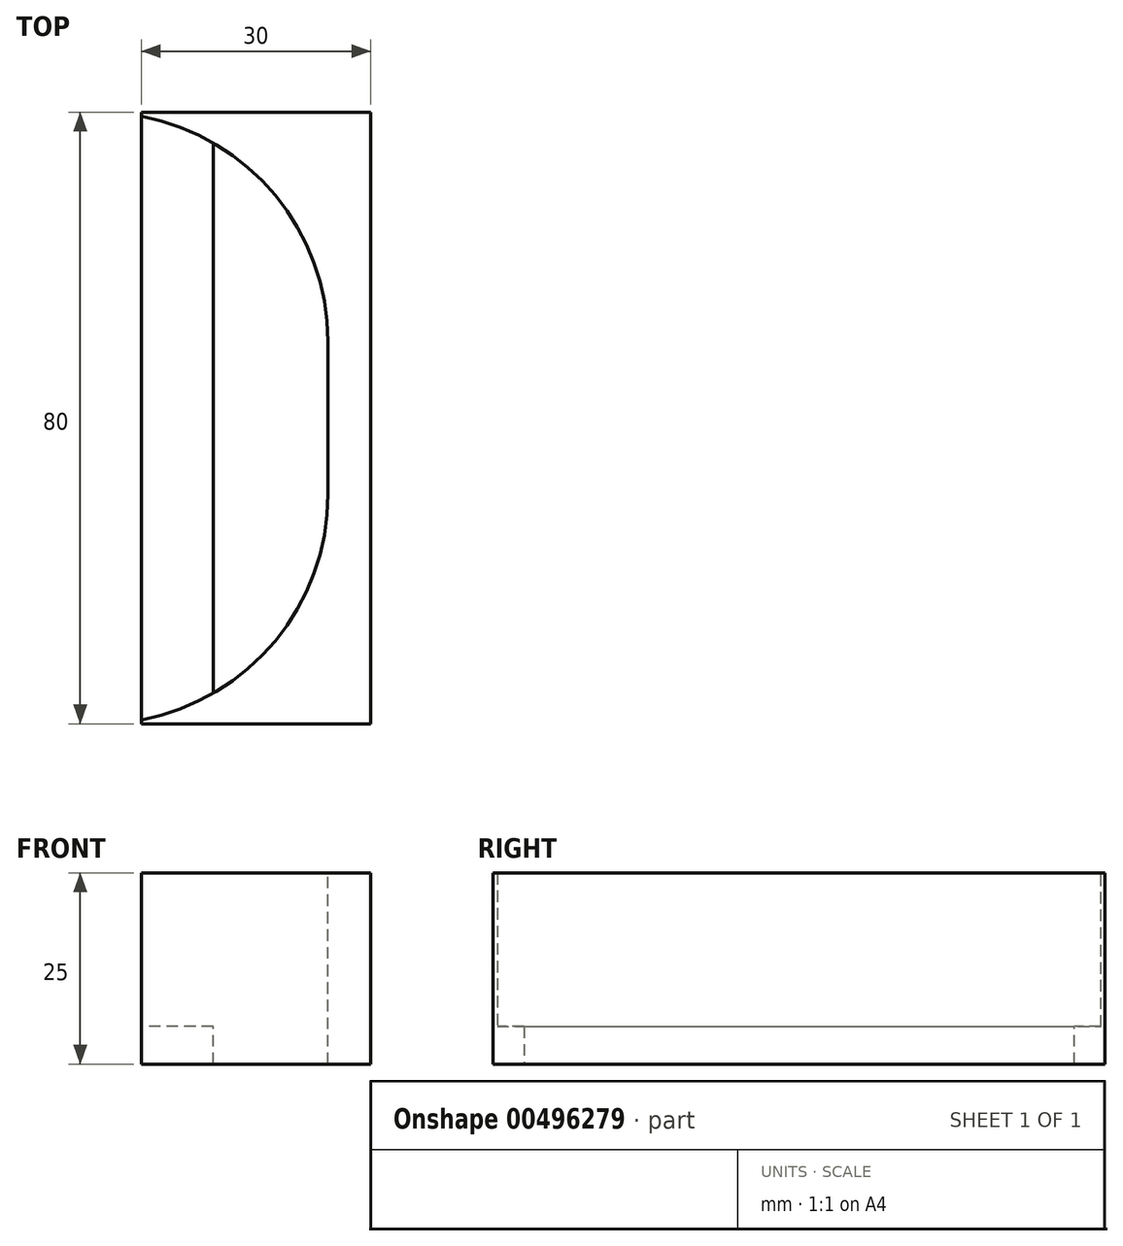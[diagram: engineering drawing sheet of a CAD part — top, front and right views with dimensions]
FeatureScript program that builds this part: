
annotation { "Feature Type Name" : "Feature", "Feature Type Description" : "" }
export const myFeature = defineFeature(function(context is Context, id is Id, definition is map)
    precondition{}
    {
        {
            var Q0;
            Q0=qCreatedBy(makeId("Front.planeOp"),FACE);
            var sketch = newSketch(context, id + "F0", { "sketchPlane" : qUnion([Q0])});
            skLineSegment(sketch, "E0.0", {"start": v(75, 129.9) * mm, "end": v(85, 129.9) * mm});
            skLineSegment(sketch, "E0.1", {"start": v(0, 0) * mm, "end": v(75, 129.9) * mm});
            skLineSegment(sketch, "E0.3", {"start": v(150, -0.1) * mm, "end": v(150, 64.9) * mm});
            skArc(sketch, "E1.filletArc", {"start": v(150, 64.9) * mm, "mid": v(130.96, 110.87) * mm, "end": v(85, 129.9) * mm});
            skLineSegment(sketch, "E2.0", {"start": v(41.28, 31.5) * mm, "end": v(86.53, 109.88) * mm});
            skArc(sketch, "E2.3", {"start": v(130, 64.9) * mm, "mid": v(117.36, 96.18) * mm, "end": v(86.53, 109.88) * mm});
            skArc(sketch, "E3", {"start": v(120, 18.9) * mm, "mid": v(127.47, 41.36) * mm, "end": v(130, 64.9) * mm});
            skPoint(sketch, "E4.visualSharp", {"position": v(34.59, 19.9) * mm});
            skArc(sketch, "E4.filletArc", {"start": v(41.28, 31.5) * mm, "mid": v(36.29, 19.45) * mm, "end": v(34.59, 6.5) * mm});
            skLineSegment(sketch, "E5", {"start": v(34.59, 4.9) * mm, "end": v(16.94, 4.9) * mm});
            skLineSegment(sketch, "E6", {"start": v(16.94, 0) * mm, "end": v(16.94, 4.9) * mm});
            skLineSegment(sketch, "E7", {"start": v(135, -0.1) * mm, "end": v(150, -0.1) * mm});
            skLineSegment(sketch, "E8", {"start": v(120, 18.9) * mm, "end": v(120, 4.9) * mm});
            skLineSegment(sketch, "E9", {"start": v(34.59, 6.5) * mm, "end": v(34.59, 4.9) * mm});
            skLineSegment(sketch, "E10", {"start": v(0, 0) * mm, "end": v(16.94, 0) * mm});
            skLineSegment(sketch, "E11", {"start": v(135, -0.1) * mm, "end": v(135, 4.9) * mm});
            skLineSegment(sketch, "E12", {"start": v(135, 4.9) * mm, "end": v(120, 4.9) * mm});
            skSolve(sketch);
        }
        {
            var Q0;
            Q0=makeQuery(id+"F0.imprint","IMPRINT",FACE,{"disambiguationData":[TD([[makeQuery(id+"F0.imprint","IMPRINT",EDGE,{"derivedFrom":sQuery(id+"F0.wireOp",EDGE,"E0.0")}),-1.0]])]});
            extrude(context, id + "F1", {"entities" : qUnion([Q0]), "depth" : 80 * mm, "offsetDistance" : 25 * mm});
        }
        {
            var Q0;
            Q0=makeQuery(id+"F1.opExtrude","CAP_EDGE",EDGE,{"disambiguationData":[OSD([sQuery(id+"F0.wireOp",EDGE,"E1.filletArc")])],"isStart":true});
            var Q1;
            Q1=makeQuery(id+"F1.opExtrude","CAP_EDGE",EDGE,{"disambiguationData":[OSD([sQuery(id+"F0.wireOp",EDGE,"E1.filletArc")])],"isStart":false});
            fillet(context, id + "F2", {"entities" : qUnion([Q0, Q1]), "radius" : 30 * mm, "tangentPropagation" : true, "allowEdgeOverflow" : false});
        }
        {
            var Q0;
            Q0=qCreatedBy(makeId("Top.planeOp"),FACE);
            var sketch = newSketch(context, id + "F3", { "sketchPlane" : qUnion([Q0])});
            skLineSegment(sketch, "E13.bottom", {"start": v(155.6, 0) * mm, "end": v(125.6, 0) * mm});
            skLineSegment(sketch, "E13.top", {"start": v(155.6, -80) * mm, "end": v(125.6, -80) * mm});
            skLineSegment(sketch, "E13.left", {"start": v(155.6, 0) * mm, "end": v(155.6, -80) * mm});
            skLineSegment(sketch, "E13.right", {"start": v(125.6, 0) * mm, "end": v(125.6, -80) * mm});
            skSolve(sketch);
        }
        {
            var Q0;
            Q0=makeQuery(id+"F3.imprint","IMPRINT",FACE,{"disambiguationData":[TD([[makeQuery(id+"F3.imprint","IMPRINT",EDGE,{"derivedFrom":sQuery(id+"F3.wireOp",EDGE,"E13.bottom")}),1.0]])]});
            extrude(context, id + "F4", {"entities" : qUnion([Q0]), "depth" : 25 * mm, "offsetDistance" : 25 * mm});
        }
        {
            var Q0;
            Q0=makeQuery(id+"F1.opExtrude","SWEPT_BODY",BODY,{"disambiguationData":[OSD([sQuery(id+"F0.wireOp",EDGE,"E0.0"),sQuery(id+"F0.wireOp",EDGE,"E0.1"),sQuery(id+"F0.wireOp",EDGE,"E0.3"),sQuery(id+"F0.wireOp",EDGE,"E1.filletArc"),sQuery(id+"F0.wireOp",EDGE,"E2.0"),sQuery(id+"F0.wireOp",EDGE,"E2.3"),sQuery(id+"F0.wireOp",EDGE,"E3"),sQuery(id+"F0.wireOp",EDGE,"E4.filletArc"),sQuery(id+"F0.wireOp",EDGE,"E5"),sQuery(id+"F0.wireOp",EDGE,"E6"),sQuery(id+"F0.wireOp",EDGE,"E7"),sQuery(id+"F0.wireOp",EDGE,"E8"),sQuery(id+"F0.wireOp",EDGE,"E9"),sQuery(id+"F0.wireOp",EDGE,"E10"),sQuery(id+"F0.wireOp",EDGE,"E11"),sQuery(id+"F0.wireOp",EDGE,"E12")])]});
            var Q1;
            Q1=makeQuery(id+"F4.opExtrude","SWEPT_BODY",BODY,{"disambiguationData":[OSD([sQuery(id+"F3.wireOp",EDGE,"E13.bottom"),sQuery(id+"F3.wireOp",EDGE,"E13.top"),sQuery(id+"F3.wireOp",EDGE,"E13.left"),sQuery(id+"F3.wireOp",EDGE,"E13.right")])]});
            booleanBodies(context, id + "F5", {"operationType" : BooleanOperationType.SUBTRACTION, "tools" : qUnion([Q0]), "targets" : qUnion([Q1])});
        }
    });
